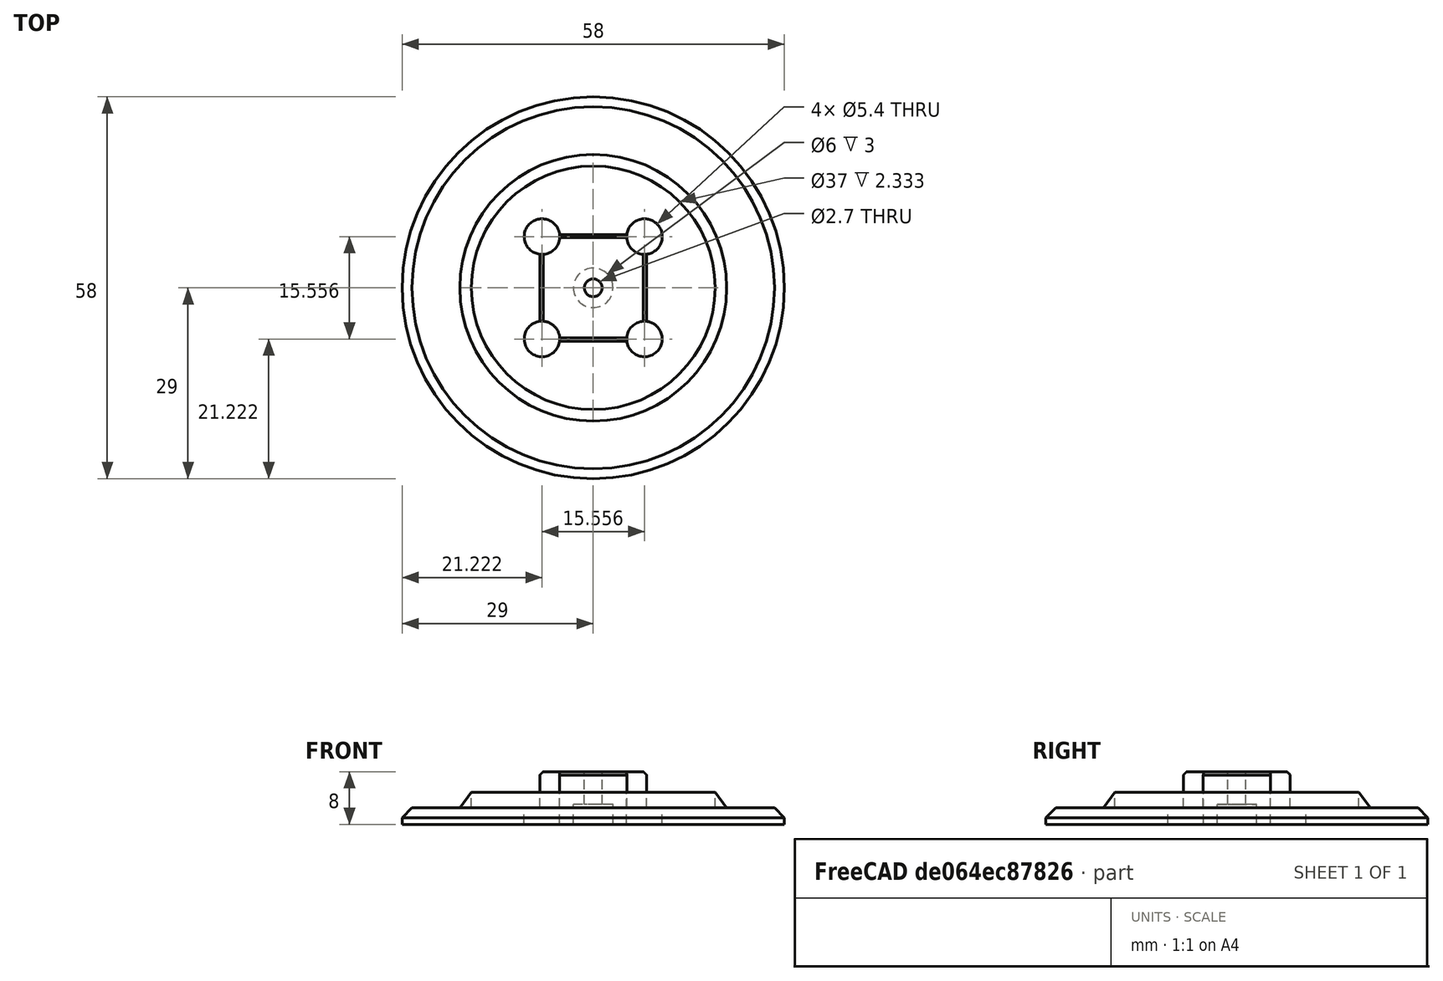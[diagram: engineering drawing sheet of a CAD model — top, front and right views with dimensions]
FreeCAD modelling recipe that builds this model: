
FCSTD DOCUMENT  (FreeCAD 0.14R2935 (Git))
Label: tendon_wheel_mx_18_29_mm_top
License: CC-BY 3.0
LicenseURL: http://creativecommons.org/licenses/by/3.0/
objects: Part::Cylinder×8, Part::MultiFuse×4, Part::Cut×3, Part::Chamfer×2, Part::Cone×1, Part::Box×1
note: 19 computed .brp shape members not serialized (recipe doc carries the construction recipe); baked Part::Feature solids carry a one-line shape summary decoded from their .brp

FEATURE [Part::Cylinder] Cylinder
  Angle = 360
  Height = 6
  Placement = pos=(0,0,2) rot=(0,0,1;0rad)
  Radius = 18.5
FEATURE [Part::Cylinder] Cylinder001
  Angle = 360
  Height = 2.5
  Placement = pos=(0,0,-0.5) rot=(0,0,1;0rad)
  Radius = 29
FEATURE [Part::Cone] Cone
  Angle = 360
  Height = 4
  Placement = pos=(0,0,1) rot=(0,0,1;0rad)
  Radius1 = 21
  Radius2 = 18
FEATURE [Part::Box] Box  label="Cube"
  Height = 5.5
  Length = 16.2
  Placement = pos=(-8.1,-8.1,2) rot=(0,0,1;0rad)
  Width = 16.2
FEATURE [Part::MultiFuse] Fusion
  Shapes = -> [Cone,Cylinder001]
FEATURE [Part::Cylinder] Cylinder002  label="Cylinder004"
  Angle = 360
  Height = 20
  Placement = pos=(0,0,-5) rot=(0,0,1;0rad)
  Radius = 1.35
FEATURE [Part::Cut] Cut
  Base = -> Fusion
  Tool = -> Cylinder
FEATURE [Part::MultiFuse] Fusion001
  Shapes = -> [Cut,Box]
FEATURE [Part::Cylinder] Cylinder003  label="Cylinder012"
  Angle = 360
  Height = 3
  Placement = pos=(0,0,-0.5) rot=(0,0,1;0rad)
  Radius = 3
FEATURE [Part::MultiFuse] Fusion002
  Shapes = -> [Cylinder003,Cylinder002]
FEATURE [Part::Cut] Cut001
  Base = -> Fusion001
  Tool = -> Fusion002
FEATURE [Part::Chamfer] Chamfer
  Base = -> Cut001
  Edges = 4 edges r=0.5: [Edge1,Edge2,Edge3,Edge4]
FEATURE [Part::Cylinder] Cylinder005  label="TopHole005"
  Angle = 360
  Height = 20
  Placement = pos=(11,0,-5) rot=(0,0,1;0rad)
  Radius = 2.7
FEATURE [Part::Cylinder] Cylinder008  label="TopHole006"
  Angle = 360
  Height = 20
  Placement = pos=(0,11,-5) rot=(0,0,1;0rad)
  Radius = 2.7
FEATURE [Part::Cylinder] Cylinder009  label="TopHole004"
  Angle = 360
  Height = 20
  Placement = pos=(-11,0,-5) rot=(0,0,1;0rad)
  Radius = 2.7
FEATURE [Part::Cylinder] Cylinder011  label="TopHole007"
  Angle = 360
  Height = 20
  Placement = pos=(0,-11,-5) rot=(0,0,1;0rad)
  Radius = 2.7
FEATURE [Part::MultiFuse] Fusion003
  Placement = pos=(0,0,0) rot=(0,0,1;0.785398rad)
  Shapes = -> [Cylinder011,Cylinder008,Cylinder009,Cylinder005]
FEATURE [Part::Cut] Cut002
  Base = -> Chamfer
  Tool = -> Fusion003
FEATURE [Part::Chamfer] Chamfer001
  Base = -> Cut002
  Edges = 1 edges r=1.5: [Edge58]
